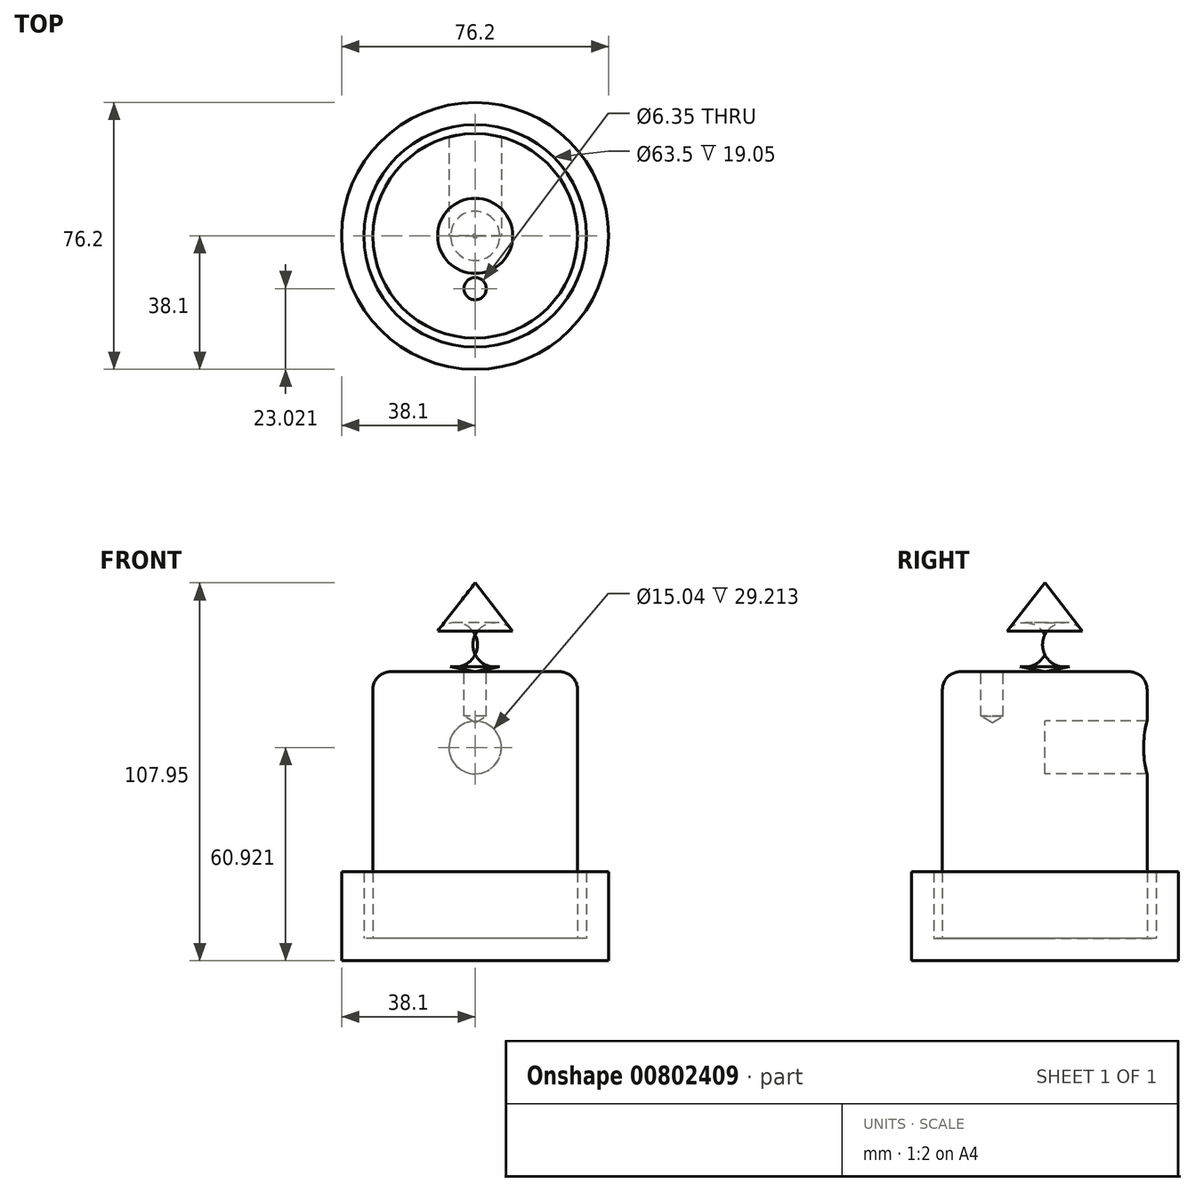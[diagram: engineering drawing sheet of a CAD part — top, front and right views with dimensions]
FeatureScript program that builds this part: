
annotation { "Feature Type Name" : "Feature", "Feature Type Description" : "" }
export const myFeature = defineFeature(function(context is Context, id is Id, definition is map)
    precondition{}
    {
        {
            var Q0;
            Q0=qCreatedBy(makeId("Top.planeOp"),FACE);
            var sketch = newSketch(context, id + "F0", { "sketchPlane" : qUnion([Q0])});
            skCircle(sketch, "E0", {"center": v(0, 0) * mm, "radius": 31.75 * mm});
            skCircle(sketch, "E1", {"center": v(0, 0) * mm, "radius": 38.1 * mm});
            skSolve(sketch);
        }
        {
            var Q0;
            Q0=makeQuery(id+"F0.imprint","IMPRINT",FACE,{"disambiguationData":[TD([[makeQuery(id+"F0.imprint","IMPRINT",EDGE,{"derivedFrom":sQuery(id+"F0.wireOp",EDGE,"E0")}),1.0]])]});
            extrude(context, id + "F1", {"entities" : qUnion([Q0]), "depth" : 6.35 * mm, "offsetDistance" : 25.4 * mm});
        }
        {
            var Q0;
            Q0=makeQuery(id+"F0.imprint","IMPRINT",FACE,{"disambiguationData":[TD([[makeQuery(id+"F0.imprint","IMPRINT",EDGE,{"derivedFrom":sQuery(id+"F0.wireOp",EDGE,"E0")}),-1.0]])]});
            extrude(context, id + "F2", {"entities" : qUnion([Q0]), "operationType" : NewBodyOperationType.ADD, "depth" : 25.4 * mm, "offsetDistance" : 25.4 * mm});
        }
        {
            var Q0;
            Q0=makeQuery(id+"F1.opExtrude","CAP_FACE",FACE,{"disambiguationData":[OSD([sQuery(id+"F0.wireOp",EDGE,"E0")])],"isStart":false});
            var sketch = newSketch(context, id + "F3", { "sketchPlane" : qUnion([Q0])});
            skCircle(sketch, "E2", {"center": v(0, 0) * mm, "radius": 29.2 * mm});
            skSolve(sketch);
        }
        {
            var Q0;
            Q0=makeQuery(id+"F3.imprint","IMPRINT",FACE,{"disambiguationData":[TD([[makeQuery(id+"F3.imprint","IMPRINT",EDGE,{"derivedFrom":sQuery(id+"F3.wireOp",EDGE,"E2")}),1.0]])]});
            extrude(context, id + "F4", {"entities" : qUnion([Q0]), "depth" : 76.2 * mm, "offsetDistance" : 25.4 * mm});
        }
        {
            var Q0;
            Q0=qCreatedBy(makeId("Right.planeOp"),FACE);
            var sketch = newSketch(context, id + "F5", { "sketchPlane" : qUnion([Q0])});
            skLineSegment(sketch, "E3", {"start": v(0, 82.55) * mm, "end": v(0, 107.95) * mm});
            skLineSegment(sketch, "E4", {"start": v(0, 107.95) * mm, "end": v(10.72, 94.17) * mm});
            skLineSegment(sketch, "E5", {"start": v(7.04, 84.06) * mm, "end": v(0, 82.55) * mm});
            skPoint(sketch, "E6.visualSharp", {"position": v(16.93, 86.18) * mm});
            skArc(sketch, "E6.filletArc", {"start": v(7.04, 84.06) * mm, "mid": v(11.67, 88.1) * mm, "end": v(10.72, 94.17) * mm});
            skSolve(sketch);
        }
        {
            var Q0;
            Q0=makeQuery(id+"F5.imprint","IMPRINT",FACE,{"disambiguationData":[TD([[makeQuery(id+"F5.imprint","IMPRINT",EDGE,{"derivedFrom":sQuery(id+"F5.wireOp",EDGE,"E3")}),-1.0]])]});
            var Q1;
            Q1=sQuery(id+"F5.wireOp",EDGE,"E3");
            revolve(context, id + "F6", {"surfaceOperationType" : NewSurfaceOperationType.NEW, "entities" : qUnion([Q0]), "axis" : qUnion([Q1]), "revolveType" : RevolveType.FULL});
        }
        {
            var Q0;
            Q0=makeQuery(id+"F4.opExtrude","CAP_EDGE",EDGE,{"disambiguationData":[OSD([sQuery(id+"F3.wireOp",EDGE,"E2")])],"isStart":false});
            fillet(context, id + "F7", {"entities" : qUnion([Q0]), "radius" : 5.08 * mm, "tangentPropagation" : true, "allowEdgeOverflow" : false});
        }
        {
            var Q0;
            Q0=makeQuery(id+"F4.opExtrude","CAP_FACE",FACE,{"disambiguationData":[OSD([sQuery(id+"F3.wireOp",EDGE,"E2")])],"isStart":false});
            var sketch = newSketch(context, id + "F8", { "sketchPlane" : qUnion([Q0])});
            skPoint(sketch, "E7", {"position": v(0, -15.08) * mm});
            skSolve(sketch);
        }
        {
            var Q0;
            Q0=qCreatedBy(makeId("Front.planeOp"),FACE);
            var sketch = newSketch(context, id + "F9", { "sketchPlane" : qUnion([Q0])});
            skCircle(sketch, "E8", {"center": v(0, 60.92) * mm, "radius": 7.52 * mm});
            skSolve(sketch);
        }
        {
            var Q0;
            Q0 = qSketchRegion(id + "F9", true);
            var Q1;
            Q1=sQuery(id+"F9.wireOp",EDGE,"E8");
            extrude(context, id + "F10", {"entities" : qUnion([Q0]), "operationType" : NewBodyOperationType.REMOVE, "surfaceEntities" : qUnion([Q1]), "oppositeDirection" : true, "depth" : 76.2 * mm, "offsetDistance" : 25.4 * mm});
        }
        {
            var Q0;
            Q0=sQuery(id+"F8.wireOp",VERTEX,"E7");
            var Q1;
            Q1=makeQuery(id+"F4.opExtrude","SWEPT_BODY",BODY,{"disambiguationData":[OSD([sQuery(id+"F3.wireOp",EDGE,"E2")])]});
            hole(context, id + "F11", {"style" : HoleStyle.SIMPLE, "endStyle" : HoleEndStyle.BLIND, "holeDiameter" : 6.35 * mm, "majorDiameter" : 6.35 * mm, "holeDepth" : 12.7 * mm, "isTappedThrough" : true, "tappedDepth" : 12.7 * mm, "tapClearance" : 3, "locations" : qUnion([Q0]), "scope" : qUnion([Q1])});
        }
    });
